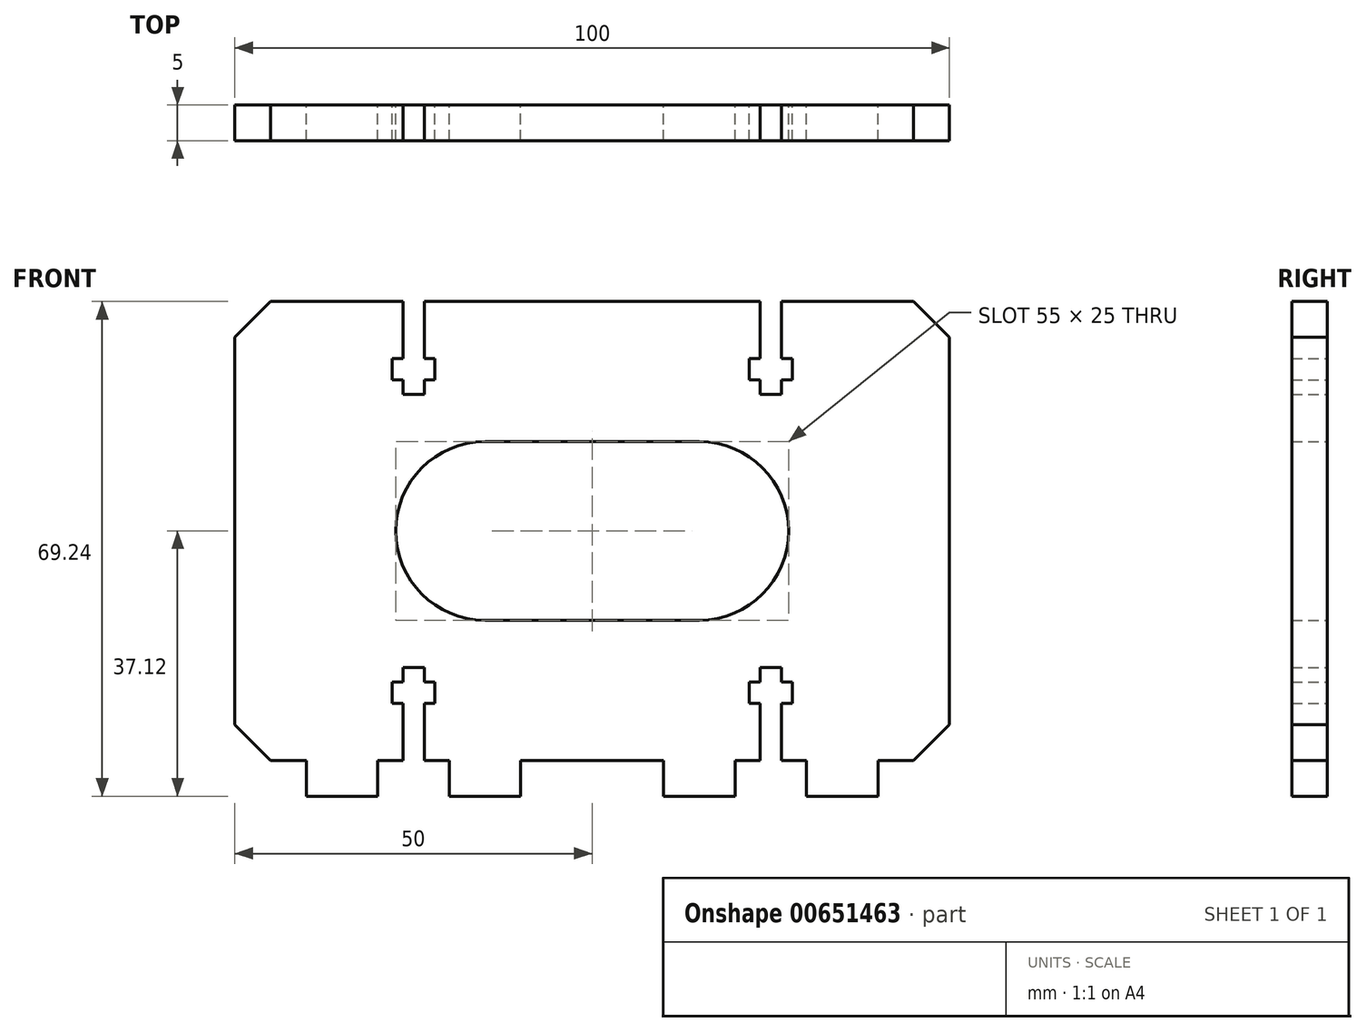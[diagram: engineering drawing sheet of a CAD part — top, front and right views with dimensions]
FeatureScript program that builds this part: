
annotation { "Feature Type Name" : "Feature", "Feature Type Description" : "" }
export const myFeature = defineFeature(function(context is Context, id is Id, definition is map)
    precondition{}
    {
        {
            var Q0;
            Q0=qCreatedBy(makeId("Front.planeOp"),FACE);
            var sketch = newSketch(context, id + "F0", { "sketchPlane" : qUnion([Q0])});
            skLineSegment(sketch, "E0.bottom", {"start": v(-50, 32.12) * mm, "end": v(50, 32.12) * mm});
            skLineSegment(sketch, "E0.top", {"start": v(-50, -32.13) * mm, "end": v(50, -32.13) * mm});
            skLineSegment(sketch, "E0.left", {"start": v(-50, 32.12) * mm, "end": v(-50, -32.13) * mm});
            skLineSegment(sketch, "E0.right", {"start": v(50, 32.12) * mm, "end": v(50, -32.13) * mm});
            skLineSegment(sketch, "E1", {"start": v(-15, 0) * mm, "end": v(15, 0) * mm});
            skArc(sketch, "E2.0.startCap", {"start": v(-15, -12.5) * mm, "mid": v(-27.5, 0) * mm, "end": v(-15, 12.5) * mm});
            skArc(sketch, "E2.0.endCap", {"start": v(15, 12.5) * mm, "mid": v(27.5, 0) * mm, "end": v(15, -12.5) * mm});
            skLineSegment(sketch, "E2.0.left", {"start": v(-15, 12.5) * mm, "end": v(15, 12.5) * mm});
            skLineSegment(sketch, "E2.0.right", {"start": v(-15, -12.5) * mm, "end": v(15, -12.5) * mm});
            skLineSegment(sketch, "E3", {"start": v(-1.5, 32.12) * mm, "end": v(-1.5, 24.12) * mm});
            skLineSegment(sketch, "E4", {"start": v(-1.5, 24.12) * mm, "end": v(-3, 24.12) * mm});
            skLineSegment(sketch, "E5", {"start": v(-3, 24.12) * mm, "end": v(-3, 21.12) * mm});
            skLineSegment(sketch, "E6", {"start": v(-3, 21.12) * mm, "end": v(-1.5, 21.12) * mm});
            skLineSegment(sketch, "E7", {"start": v(-1.5, 21.12) * mm, "end": v(-1.5, 19.13) * mm});
            skLineSegment(sketch, "E8", {"start": v(-1.5, 19.13) * mm, "end": v(0, 19.13) * mm});
            skLineSegment(sketch, "E9", {"start": v(0, 19.13) * mm, "end": v(0, 38.2) * mm, "construction": true});
            skLineSegment(sketch, "E10.MirrorCS", {"start": v(1.5, 32.12) * mm, "end": v(1.5, 24.12) * mm});
            skLineSegment(sketch, "E11.MirrorCS", {"start": v(1.5, 24.12) * mm, "end": v(3, 24.12) * mm});
            skLineSegment(sketch, "E12.MirrorCS", {"start": v(3, 24.12) * mm, "end": v(3, 21.12) * mm});
            skLineSegment(sketch, "E13.MirrorCS", {"start": v(3, 21.12) * mm, "end": v(1.5, 21.12) * mm});
            skLineSegment(sketch, "E14.MirrorCS", {"start": v(1.5, 21.12) * mm, "end": v(1.5, 19.13) * mm});
            skLineSegment(sketch, "E15.MirrorCS", {"start": v(1.5, 19.13) * mm, "end": v(0, 19.13) * mm});
            skLineSegment(sketch, "E16.MirrorCS", {"start": v(-1.5, -32.12) * mm, "end": v(-1.5, -24.12) * mm});
            skLineSegment(sketch, "E17.MirrorCS", {"start": v(-1.5, -24.12) * mm, "end": v(-3, -24.12) * mm});
            skLineSegment(sketch, "E18.MirrorCS", {"start": v(-3, -24.12) * mm, "end": v(-3, -21.12) * mm});
            skLineSegment(sketch, "E19.MirrorCS", {"start": v(-3, -21.12) * mm, "end": v(-1.5, -21.12) * mm});
            skLineSegment(sketch, "E20.MirrorCS", {"start": v(-1.5, -21.12) * mm, "end": v(-1.5, -19.13) * mm});
            skLineSegment(sketch, "E21.MirrorCS", {"start": v(-1.5, -19.13) * mm, "end": v(0, -19.13) * mm});
            skLineSegment(sketch, "E22.MirrorCS", {"start": v(1.5, -19.13) * mm, "end": v(0, -19.13) * mm});
            skLineSegment(sketch, "E23.MirrorCS", {"start": v(1.5, -21.12) * mm, "end": v(1.5, -19.13) * mm});
            skLineSegment(sketch, "E24.MirrorCS", {"start": v(3, -21.12) * mm, "end": v(1.5, -21.12) * mm});
            skLineSegment(sketch, "E25.MirrorCS", {"start": v(3, -24.12) * mm, "end": v(3, -21.12) * mm});
            skLineSegment(sketch, "E26.MirrorCS", {"start": v(1.5, -24.12) * mm, "end": v(3, -24.12) * mm});
            skLineSegment(sketch, "E27.MirrorCS", {"start": v(1.5, -32.12) * mm, "end": v(1.5, -24.12) * mm});
            skLineSegment(sketch, "E28.1.0.0", {"start": v(26.5, 32.12) * mm, "end": v(26.5, 24.12) * mm});
            skLineSegment(sketch, "E28.1.0.1", {"start": v(23.5, 32.12) * mm, "end": v(23.5, 24.12) * mm});
            skLineSegment(sketch, "E28.1.0.2", {"start": v(23.5, 24.12) * mm, "end": v(22, 24.12) * mm});
            skLineSegment(sketch, "E28.1.0.3", {"start": v(22, 24.12) * mm, "end": v(22, 21.12) * mm});
            skLineSegment(sketch, "E28.1.0.4", {"start": v(22, 21.12) * mm, "end": v(23.5, 21.12) * mm});
            skLineSegment(sketch, "E28.1.0.5", {"start": v(23.5, 21.12) * mm, "end": v(23.5, 19.13) * mm});
            skLineSegment(sketch, "E28.1.0.6", {"start": v(23.5, 19.13) * mm, "end": v(25, 19.13) * mm});
            skLineSegment(sketch, "E28.1.0.7", {"start": v(26.5, 19.13) * mm, "end": v(25, 19.13) * mm});
            skLineSegment(sketch, "E28.1.0.8", {"start": v(26.5, 21.12) * mm, "end": v(26.5, 19.13) * mm});
            skLineSegment(sketch, "E28.1.0.9", {"start": v(28, 21.12) * mm, "end": v(26.5, 21.12) * mm});
            skLineSegment(sketch, "E28.1.0.10", {"start": v(28, 24.12) * mm, "end": v(28, 21.12) * mm});
            skLineSegment(sketch, "E28.1.0.11", {"start": v(26.5, 24.12) * mm, "end": v(28, 24.12) * mm});
            skLineSegment(sketch, "E28.direction1", {"start": v(1.5, 24.12) * mm, "end": v(26.5, 24.12) * mm, "construction": true});
            skLineSegment(sketch, "E29.MirrorCS", {"start": v(-26.5, 32.12) * mm, "end": v(-26.5, 24.12) * mm});
            skLineSegment(sketch, "E30.MirrorCS", {"start": v(-23.5, 32.12) * mm, "end": v(-23.5, 24.12) * mm});
            skLineSegment(sketch, "E31.MirrorCS", {"start": v(-23.5, 24.12) * mm, "end": v(-22, 24.12) * mm});
            skLineSegment(sketch, "E32.MirrorCS", {"start": v(-22, 24.12) * mm, "end": v(-22, 21.12) * mm});
            skLineSegment(sketch, "E33.MirrorCS", {"start": v(-22, 21.12) * mm, "end": v(-23.5, 21.12) * mm});
            skLineSegment(sketch, "E34.MirrorCS", {"start": v(-23.5, 21.12) * mm, "end": v(-23.5, 19.13) * mm});
            skLineSegment(sketch, "E35.MirrorCS", {"start": v(-23.5, 19.13) * mm, "end": v(-25, 19.13) * mm});
            skLineSegment(sketch, "E36.MirrorCS", {"start": v(-26.5, 19.13) * mm, "end": v(-25, 19.13) * mm});
            skLineSegment(sketch, "E37.MirrorCS", {"start": v(-26.5, 21.12) * mm, "end": v(-26.5, 19.13) * mm});
            skLineSegment(sketch, "E38.MirrorCS", {"start": v(-28, 21.12) * mm, "end": v(-26.5, 21.12) * mm});
            skLineSegment(sketch, "E39.MirrorCS", {"start": v(-28, 24.12) * mm, "end": v(-28, 21.12) * mm});
            skLineSegment(sketch, "E40.MirrorCS", {"start": v(-26.5, 24.12) * mm, "end": v(-28, 24.12) * mm});
            skLineSegment(sketch, "E41.MirrorCS", {"start": v(-26.5, -32.12) * mm, "end": v(-26.5, -24.12) * mm});
            skLineSegment(sketch, "E42.MirrorCS", {"start": v(-26.5, -24.12) * mm, "end": v(-28, -24.12) * mm});
            skLineSegment(sketch, "E43.MirrorCS", {"start": v(-28, -24.12) * mm, "end": v(-28, -21.12) * mm});
            skLineSegment(sketch, "E44.MirrorCS", {"start": v(-28, -21.12) * mm, "end": v(-26.5, -21.12) * mm});
            skLineSegment(sketch, "E45.MirrorCS", {"start": v(-26.5, -21.12) * mm, "end": v(-26.5, -19.13) * mm});
            skLineSegment(sketch, "E46.MirrorCS", {"start": v(-26.5, -19.13) * mm, "end": v(-25, -19.13) * mm});
            skLineSegment(sketch, "E47.MirrorCS", {"start": v(-23.5, -19.13) * mm, "end": v(-25, -19.13) * mm});
            skLineSegment(sketch, "E48.MirrorCS", {"start": v(-23.5, -21.12) * mm, "end": v(-23.5, -19.13) * mm});
            skLineSegment(sketch, "E49.MirrorCS", {"start": v(-22, -21.12) * mm, "end": v(-23.5, -21.12) * mm});
            skLineSegment(sketch, "E50.MirrorCS", {"start": v(-22, -24.12) * mm, "end": v(-22, -21.12) * mm});
            skLineSegment(sketch, "E51.MirrorCS", {"start": v(-23.5, -24.12) * mm, "end": v(-22, -24.12) * mm});
            skLineSegment(sketch, "E52.MirrorCS", {"start": v(-23.5, -32.12) * mm, "end": v(-23.5, -24.12) * mm});
            skLineSegment(sketch, "E53.MirrorCS", {"start": v(26.5, -32.12) * mm, "end": v(26.5, -24.12) * mm});
            skLineSegment(sketch, "E54.MirrorCS", {"start": v(26.5, -24.12) * mm, "end": v(28, -24.12) * mm});
            skLineSegment(sketch, "E55.MirrorCS", {"start": v(28, -24.12) * mm, "end": v(28, -21.12) * mm});
            skLineSegment(sketch, "E56.MirrorCS", {"start": v(28, -21.12) * mm, "end": v(26.5, -21.12) * mm});
            skLineSegment(sketch, "E57.MirrorCS", {"start": v(26.5, -21.12) * mm, "end": v(26.5, -19.13) * mm});
            skLineSegment(sketch, "E58.MirrorCS", {"start": v(26.5, -19.13) * mm, "end": v(25, -19.13) * mm});
            skLineSegment(sketch, "E59.MirrorCS", {"start": v(23.5, -19.13) * mm, "end": v(25, -19.13) * mm});
            skLineSegment(sketch, "E60.MirrorCS", {"start": v(23.5, -21.12) * mm, "end": v(23.5, -19.13) * mm});
            skLineSegment(sketch, "E61.MirrorCS", {"start": v(22, -21.12) * mm, "end": v(23.5, -21.12) * mm});
            skLineSegment(sketch, "E62.MirrorCS", {"start": v(22, -24.12) * mm, "end": v(22, -21.12) * mm});
            skLineSegment(sketch, "E63.MirrorCS", {"start": v(23.5, -24.12) * mm, "end": v(22, -24.12) * mm});
            skLineSegment(sketch, "E64.MirrorCS", {"start": v(23.5, -32.12) * mm, "end": v(23.5, -24.12) * mm});
            skSolve(sketch);
        }
        {
            var Q0;
            Q0=makeQuery(id+"F0.imprint","IMPRINT",FACE,{"disambiguationData":[TD([[makeQuery(id+"F0.imprint","IMPRINT",EDGE,{"derivedFrom":sQuery(id+"F0.wireOp",EDGE,"E0.bottom")}),-1.0]])]});
            var Q1;
            {var subQ1=sQuery(id+"F0.wireOp",EDGE,"E3");Q1=makeQuery(id+"F0.imprint","IMPRINT",FACE,{"disambiguationData":[TD([[makeQuery(id+"F0.imprint","IMPRINT",EDGE,{"derivedFrom":subQ1}),1.0]])]});}
            var Q2;
            {var subQ0=sQuery(id+"F0.wireOp",EDGE,"E16.MirrorCS");Q2=makeQuery(id+"F0.imprint","IMPRINT",FACE,{"disambiguationData":[TD([[makeQuery(id+"F0.imprint","IMPRINT",EDGE,{"derivedFrom":subQ0}),-1.0]])]});}
            extrude(context, id + "F1", {"entities" : qUnion([Q0, Q1, Q2]), "depth" : 5 * mm, "offsetDistance" : 25 * mm});
        }
        {
            var Q0;
            Q0=makeQuery(id+"F1.opExtrude","SWEPT_EDGE",EDGE,{"disambiguationData":[OSD([sQuery(id+"F0.wireOp",EDGE,"E0.bottom"),sQuery(id+"F0.wireOp",EDGE,"E0.left")])]});
            var Q1;
            Q1=makeQuery(id+"F1.opExtrude","SWEPT_EDGE",EDGE,{"disambiguationData":[OSD([sQuery(id+"F0.wireOp",EDGE,"E0.bottom"),sQuery(id+"F0.wireOp",EDGE,"E0.right")])]});
            var Q2;
            Q2=makeQuery(id+"F1.opExtrude","SWEPT_EDGE",EDGE,{"disambiguationData":[OSD([sQuery(id+"F0.wireOp",EDGE,"E0.top"),sQuery(id+"F0.wireOp",EDGE,"E0.left")])]});
            var Q3;
            Q3=makeQuery(id+"F1.opExtrude","SWEPT_EDGE",EDGE,{"disambiguationData":[OSD([sQuery(id+"F0.wireOp",EDGE,"E0.top"),sQuery(id+"F0.wireOp",EDGE,"E0.right")])]});
            chamfer(context, id + "F2", {"entities" : qUnion([Q0, Q1, Q2, Q3]), "width" : 5 * mm, "tangentPropagation" : true});
        }
        {
            var Q0;
            Q0=makeQuery(id+"F1.opExtrude","SWEPT_FACE",FACE,{"disambiguationData":[OSD([sQuery(id+"F0.wireOp",EDGE,"E0.top")])]});
            var sketch = newSketch(context, id + "F3", { "sketchPlane" : qUnion([Q0])});
            skLineSegment(sketch, "E65.bottom", {"start": v(-40, 5) * mm, "end": v(-30, 5) * mm});
            skLineSegment(sketch, "E65.top", {"start": v(-40, 0) * mm, "end": v(-30, 0) * mm});
            skLineSegment(sketch, "E65.left", {"start": v(-40, 5) * mm, "end": v(-40, 0) * mm});
            skLineSegment(sketch, "E65.right", {"start": v(-30, 5) * mm, "end": v(-30, 0) * mm});
            skLineSegment(sketch, "E66.bottom", {"start": v(-20, 5) * mm, "end": v(-10, 5) * mm});
            skLineSegment(sketch, "E66.top", {"start": v(-20, 0) * mm, "end": v(-10, 0) * mm});
            skLineSegment(sketch, "E66.left", {"start": v(-20, 5) * mm, "end": v(-20, 0) * mm});
            skLineSegment(sketch, "E66.right", {"start": v(-10, 5) * mm, "end": v(-10, 0) * mm});
            skLineSegment(sketch, "E67.bottom", {"start": v(10, 5) * mm, "end": v(20, 5) * mm});
            skLineSegment(sketch, "E67.top", {"start": v(10, 0) * mm, "end": v(20, 0) * mm});
            skLineSegment(sketch, "E67.left", {"start": v(10, 5) * mm, "end": v(10, 0) * mm});
            skLineSegment(sketch, "E67.right", {"start": v(20, 5) * mm, "end": v(20, 0) * mm});
            skLineSegment(sketch, "E68.bottom", {"start": v(30, 5) * mm, "end": v(40, 5) * mm});
            skLineSegment(sketch, "E68.top", {"start": v(30, 0) * mm, "end": v(40, 0) * mm});
            skLineSegment(sketch, "E68.left", {"start": v(30, 5) * mm, "end": v(30, 0) * mm});
            skLineSegment(sketch, "E68.right", {"start": v(40, 5) * mm, "end": v(40, 0) * mm});
            skLineSegment(sketch, "E69", {"start": v(-25, 9.91) * mm, "end": v(-25, -12.22) * mm, "construction": true});
            skLineSegment(sketch, "E70", {"start": v(25, 10.76) * mm, "end": v(25, -11.94) * mm, "construction": true});
            skSolve(sketch);
        }
        {
            var Q0;
            Q0=makeQuery(id+"F3.imprint","IMPRINT",FACE,{"disambiguationData":[TD([[makeQuery(id+"F3.imprint","IMPRINT",EDGE,{"derivedFrom":sQuery(id+"F3.wireOp",EDGE,"E68.bottom")}),-1.0]])]});
            var Q1;
            Q1=makeQuery(id+"F3.imprint","IMPRINT",FACE,{"disambiguationData":[TD([[makeQuery(id+"F3.imprint","IMPRINT",EDGE,{"derivedFrom":sQuery(id+"F3.wireOp",EDGE,"E67.bottom")}),-1.0]])]});
            var Q2;
            Q2=makeQuery(id+"F3.imprint","IMPRINT",FACE,{"disambiguationData":[TD([[makeQuery(id+"F3.imprint","IMPRINT",EDGE,{"derivedFrom":sQuery(id+"F3.wireOp",EDGE,"E66.bottom")}),-1.0]])]});
            var Q3;
            Q3=makeQuery(id+"F3.imprint","IMPRINT",FACE,{"disambiguationData":[TD([[makeQuery(id+"F3.imprint","IMPRINT",EDGE,{"derivedFrom":sQuery(id+"F3.wireOp",EDGE,"E65.bottom")}),-1.0]])]});
            extrude(context, id + "F4", {"entities" : qUnion([Q0, Q1, Q2, Q3]), "operationType" : NewBodyOperationType.ADD, "depth" : 5 * mm, "offsetDistance" : 25 * mm});
        }
    });
